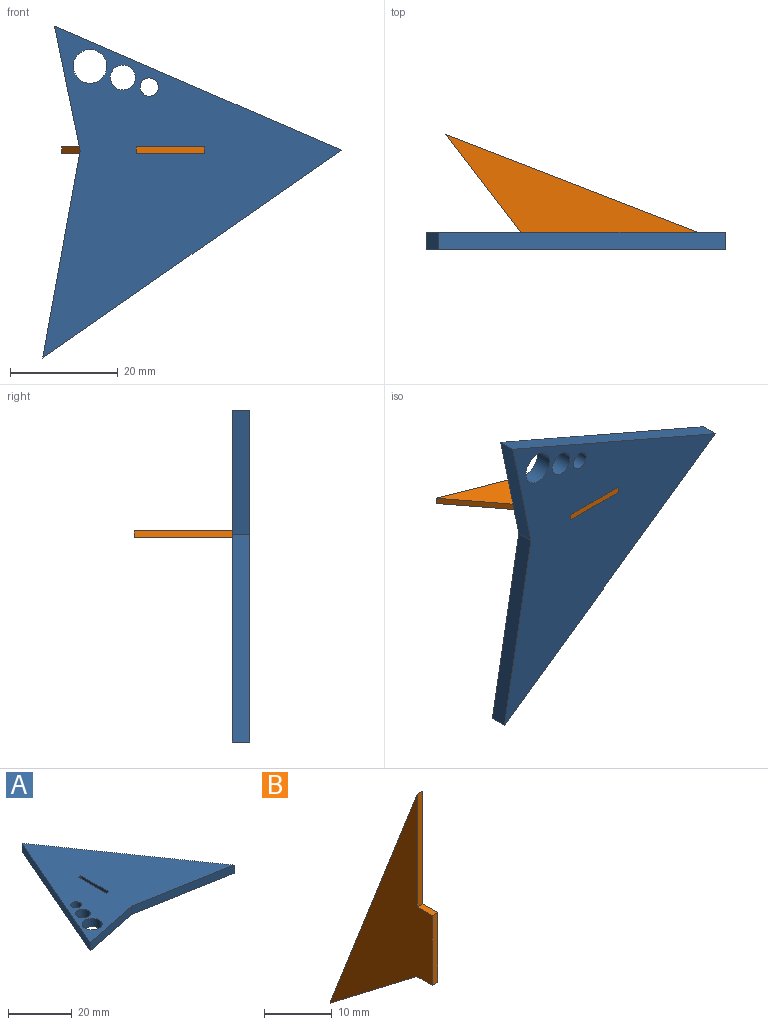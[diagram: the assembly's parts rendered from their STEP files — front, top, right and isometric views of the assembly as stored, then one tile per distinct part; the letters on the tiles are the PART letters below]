
ASSEMBLY  parts=2 mates=1
PART A: 13 faces, bbox 61.8x55.5x3.2 mm
  f0: plane 12.63x3.18mm, normal (-1,0,0), area 40.1mm2, adj f1,f10,f11,f12
  f1: plane 3.18x1.19mm, normal (0,1,0), area 3.8mm2, adj f0,f2,f11,f12
  f2: plane 12.63x3.18mm, normal (1,0,0), area 40.1mm2, adj f1,f10,f11,f12
  f3: plane 55.54x38.68mm, normal (0.82,0.57,0), area 214.9mm2, adj f4,f6,f11,f12
  f4: plane 53.34x23.1mm, normal (-0.92,0.4,0), area 184.5mm2, adj f3,f5,f11,f12
  f5: plane 23.1x4.77mm, normal (0.2,-0.98,0), area 74.9mm2, adj f4,f6,f11,f12
  f6: plane 38.68x6.97mm, normal (-0.18,-0.98,0), area 124.8mm2, adj f3,f5,f11,f12
  f7: cylinder r=1.69mm len=3.38mm, axis (0,0,-1), area 33.7mm2, adj f11,f12
  f8: cylinder r=2.32mm len=4.64mm, axis (0,0,-1), area 46.3mm2, adj f11,f12
  f9: cylinder r=3.12mm len=6.23mm, axis (0,0,-1), area 62.2mm2, adj f11,f12
  f10: plane 3.18x1.19mm, normal (0,-1,0), area 3.8mm2, adj f0,f2,f11,f12
  f11: plane 61.77x55.54mm, normal (0,0,1), area 1428.8mm2, adj f0,f1,f2,f3,f4,f5,f6,f7
  f12: plane 61.77x55.54mm, normal (0,0,-1), area 1428.8mm2, adj f0,f1,f2,f3,f4,f5,f6,f7
PART B: 8 faces, bbox 1.2x21.4x46.9 mm
  f0: plane 12.62x1.19mm, normal (0,-1,0), area 15mm2, adj f1,f5,f6,f7
  f1: plane 3.21x1.19mm, normal (0,0,-1), area 3.8mm2, adj f0,f2,f6,f7
  f2: plane 18.17x13.87mm, normal (0,-0.61,-0.79), area 27.2mm2, adj f1,f3,f6,f7
  f3: plane 46.91x18.21mm, normal (0,0.93,0.36), area 59.9mm2, adj f2,f4,f6,f7
  f4: plane 20.42x1.19mm, normal (0,-1,0), area 24.3mm2, adj f3,f5,f6,f7
  f5: plane 3.17x1.19mm, normal (0,0,1), area 3.8mm2, adj f0,f4,f6,f7
  f6: plane 46.91x21.38mm, normal (1,0,0), area 340.6mm2, adj f0,f1,f2,f3,f4,f5
  f7: plane 46.91x21.38mm, normal (-1,0,0), area 340.6mm2, adj f0,f1,f2,f3,f4,f5
PLACE A rot(axis=(0.58,0.58,-0.58),120deg) t=(-74.74,0.46,-12.23)mm
PLACE B rot(axis=(0,1,0),90deg) t=(-59.16,-2.7,-11.63)mm
MATE planar B.f1 <-> A.f1  axis (-1,0,0) through (-68.07,-1.09,-12.23)mm
